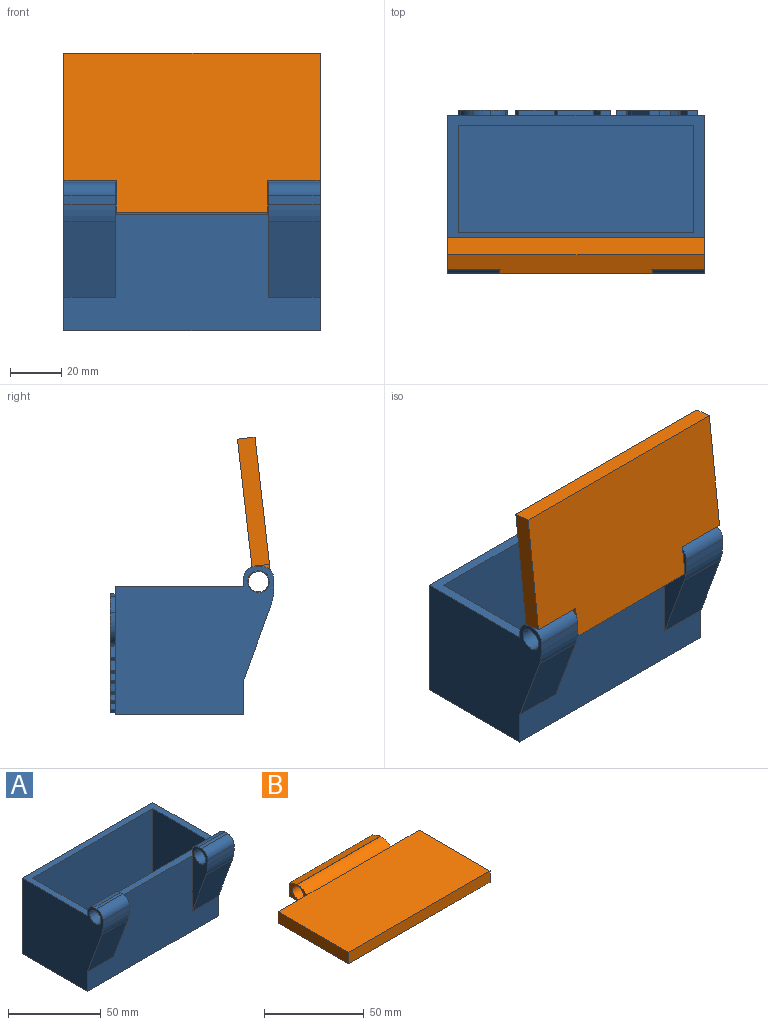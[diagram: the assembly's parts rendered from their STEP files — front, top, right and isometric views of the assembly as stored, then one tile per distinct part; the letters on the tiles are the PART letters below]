
ASSEMBLY  parts=2 mates=1
PART A: 93 faces, bbox 100x64x58 mm
  f0: plane 62x58mm, normal (-1,0,0), area 2773.6mm2, adj f1,f3,f4,f5,f10,f11,f13,f19
  f1: plane 100x50mm, normal (0,0,-1), area 5000mm2, adj f0,f2,f4,f5
  f2: plane 62x58mm, normal (1,0,0), area 2773.6mm2, adj f1,f3,f4,f5,f6,f8,f9,f20
  f3: plane 100x50mm, normal (0,0,1), area 1136mm2, adj f0,f2,f4,f5,f6,f10,f14,f15
  f4: plane 100x50mm, normal (0,-1,0), area 3521.2mm2, adj f0,f1,f2,f3,f7,f12,f21,f22
  f5: plane 100x50mm, normal (0,1,0), area 4050.1mm2, adj f0,f1,f2,f3,f29,f30,f31,f32
  f6: plane 20x3mm, normal (0,1,0), area 60mm2, adj f2,f3,f7,f28
  f7: plane 44.97x12mm, normal (-1,0,0), area 273.6mm2, adj f4,f6,f8,f9,f20,f22,f24,f27
  f8: plane 20x3.47mm, normal (0,-1,0), area 69.5mm2, adj f2,f7,f24,f27
  f9: plane 20x2mm, normal (0,0,1), area 40mm2, adj f2,f7,f27,f28
  f10: plane 20x3mm, normal (0,1,0), area 60mm2, adj f0,f3,f12,f26
  f11: plane 20x3.47mm, normal (0,-1,0), area 69.5mm2, adj f0,f12,f23,f25
  f12: plane 44.97x12mm, normal (1,0,0), area 273.6mm2, adj f4,f10,f11,f13,f19,f21,f23,f25
  f13: plane 20x2mm, normal (0,0,1), area 40mm2, adj f0,f12,f25,f26
  f14: plane 92x46mm, normal (0,-1,0), area 4232mm2, adj f3,f16,f17,f18
  f15: plane 92x46mm, normal (0,1,0), area 4232mm2, adj f3,f16,f17,f18
  f16: plane 46x42mm, normal (-1,0,0), area 1932mm2, adj f3,f14,f15,f17
  f17: plane 92x42mm, normal (0,0,1), area 3864mm2, adj f14,f15,f16,f18
  f18: plane 46x42mm, normal (1,0,0), area 1932mm2, adj f3,f14,f15,f17
  f19: cylinder r=4.25mm len=20mm, axis (1,0,0), area 534.1mm2, adj f0,f12
  f20: cylinder r=4.25mm len=20mm, axis (1,0,0), area 534.1mm2, adj f2,f7
  f21: plane 29.66x20mm, normal (0,-0.94,-0.34), area 631.2mm2, adj f0,f4,f12,f23
  f22: plane 29.66x20mm, normal (0,-0.94,-0.34), area 631.2mm2, adj f2,f4,f7,f24
  f23: cylinder r=20mm len=20mm, axis (1,0,0), area 139.6mm2, adj f0,f11,f12,f21
  f24: cylinder r=20mm len=20mm, axis (1,0,0), area 139.6mm2, adj f2,f7,f8,f22
  f25: cylinder r=5mm len=20mm, axis (-1,0,0), area 157.1mm2, adj f0,f11,f12,f13
  f26: cylinder r=5mm len=20mm, axis (1,0,0), area 157.1mm2, adj f0,f10,f12,f13
  f27: cylinder r=5mm len=20mm, axis (-1,0,0), area 157.1mm2, adj f2,f7,f8,f9
  f28: cylinder r=5mm len=20mm, axis (1,0,0), area 157.1mm2, adj f2,f6,f7,f9
  f29: plane 9.98x8.17mm, normal (-0.63,0,0.77), area 25.8mm2, adj f5,f30,f41,f42
  f30: plane 10.38x3.74mm, normal (-0.94,0,-0.34), area 22.1mm2, adj f5,f29,f31,f42
  f31: plane 4.37x2mm, normal (0.32,0,0.95), area 9.2mm2, adj f5,f30,f32,f42
  f32: plane 7.99x2.92mm, normal (0.94,0,0.34), area 17mm2, adj f5,f31,f33,f42
  f33: plane 2.7x2mm, normal (0.96,0,0.29), area 5.6mm2, adj f5,f32,f34,f42
  f34: plane 8.5x2.83mm, normal (-0.95,0,0.32), area 17.9mm2, adj f5,f33,f35,f42
  f35: plane 3.94x2mm, normal (0.32,0,0.95), area 8.3mm2, adj f5,f34,f36,f42
  f36: plane 18.56x6.19mm, normal (0.95,0,-0.32), area 39.1mm2, adj f5,f35,f37,f42
  f37: plane 3.94x2mm, normal (-0.32,0,-0.95), area 8.3mm2, adj f5,f36,f38,f42
  f38: plane 6.63x2.21mm, normal (-0.95,0,0.32), area 14mm2, adj f5,f37,f39,f42
  f39: plane 2x1.75mm, normal (-0.81,0,-0.59), area 4.3mm2, adj f5,f38,f40,f42
  f40: plane 7.47x6.2mm, normal (0.64,0,-0.77), area 19.4mm2, adj f5,f39,f41,f42
  f41: plane 4.47x2mm, normal (-0.32,0,-0.95), area 9.4mm2, adj f5,f29,f40,f42
  f42: plane 23.53x21.12mm, normal (0,1,0), area 175.6mm2, adj f29,f30,f31,f32,f33,f34,f35,f36
  f43: plane 12.22x2mm, normal (1,0,-0.01), area 24.4mm2, adj f5,f44,f52,f53
  f44: extruded ~4.41x2mm, area 8.9mm2, adj f5,f43,f45,f53
  f45: extruded ~2x1.68mm, area 3.9mm2, adj f5,f44,f46,f53
  f46: extruded ~2.08x2mm, area 5mm2, adj f5,f45,f47,f53
  f47: plane 9.88x7.18mm, normal (-0.81,0,0.59), area 24.4mm2, adj f5,f46,f48,f53
  f48: plane 3.97x2mm, normal (0.32,0,0.95), area 8.4mm2, adj f5,f47,f49,f53
  f49: plane 16.46x12.49mm, normal (0.8,0,-0.6), area 41.3mm2, adj f5,f48,f50,f53
  f50: plane 4.29x2mm, normal (-0.32,0,-0.95), area 9mm2, adj f5,f49,f51,f53
  f51: plane 20.67x2mm, normal (-1,0,-0.01), area 41.3mm2, adj f5,f50,f52,f53
  f52: plane 3.97x2mm, normal (0.32,0,0.95), area 8.4mm2, adj f5,f43,f51,f53
  f53: plane 22.1x16.9mm, normal (0,1,0), area 147.6mm2, adj f43,f44,f45,f46,f47,f48,f49,f50
  f54: plane 3.94x2mm, normal (-0.32,0,-0.95), area 8.3mm2, adj f5,f55,f57,f58
  f55: plane 18.56x6.19mm, normal (-0.95,0,0.32), area 39.1mm2, adj f5,f54,f56,f58
  f56: plane 3.94x2mm, normal (0.32,0,0.95), area 8.3mm2, adj f5,f55,f57,f58
  f57: plane 18.56x6.19mm, normal (0.95,0,-0.32), area 39.1mm2, adj f5,f54,f56,f58
  f58: plane 19.88x10.13mm, normal (0,1,0), area 81.2mm2, adj f54,f55,f56,f57
  f59: plane 15.29x5.1mm, normal (-0.95,0,0.32), area 32.2mm2, adj f5,f60,f66,f67
  f60: plane 5.04x2mm, normal (-0.32,0,-0.95), area 10.6mm2, adj f5,f59,f61,f67
  f61: plane 3.27x2mm, normal (-0.95,0,0.32), area 6.9mm2, adj f5,f60,f62,f67
  f62: plane 14.02x4.68mm, normal (0.32,0,0.95), area 29.6mm2, adj f5,f61,f63,f67
  f63: plane 3.27x2mm, normal (0.95,0,-0.32), area 6.9mm2, adj f5,f62,f64,f67
  f64: plane 5.04x2mm, normal (-0.32,0,-0.95), area 10.6mm2, adj f5,f63,f65,f67
  f65: plane 15.29x5.1mm, normal (0.95,0,-0.32), area 32.2mm2, adj f5,f64,f66,f67
  f66: plane 3.94x2mm, normal (-0.32,0,-0.95), area 8.3mm2, adj f5,f59,f65,f67
  f67: plane 21.56x15.17mm, normal (0,1,0), area 117.9mm2, adj f59,f60,f61,f62,f63,f64,f65,f66
  f68: plane 15.29x5.1mm, normal (-0.95,0,0.32), area 32.2mm2, adj f5,f69,f75,f76
  f69: plane 5.04x2mm, normal (-0.32,0,-0.95), area 10.6mm2, adj f5,f68,f70,f76
  f70: plane 3.27x2mm, normal (-0.95,0,0.32), area 6.9mm2, adj f5,f69,f71,f76
  f71: plane 14.02x4.68mm, normal (0.32,0,0.95), area 29.6mm2, adj f5,f70,f72,f76
  f72: plane 3.27x2mm, normal (0.95,0,-0.32), area 6.9mm2, adj f5,f71,f73,f76
  f73: plane 5.04x2mm, normal (-0.32,0,-0.95), area 10.6mm2, adj f5,f72,f74,f76
  f74: plane 15.29x5.1mm, normal (0.95,0,-0.32), area 32.2mm2, adj f5,f73,f75,f76
  f75: plane 3.94x2mm, normal (-0.32,0,-0.95), area 8.3mm2, adj f5,f68,f74,f76
  f76: plane 21.56x15.17mm, normal (0,1,0), area 117.9mm2, adj f68,f69,f70,f71,f72,f73,f74,f75
  f77: extruded ~6.33x4.63mm, area 16.1mm2, adj f5,f78,f90,f91
  f78: extruded ~7.37x2mm, area 15.2mm2, adj f5,f77,f79,f91
  f79: extruded ~5.75x4.64mm, area 15.2mm2, adj f5,f78,f80,f91
  f80: extruded ~7.84x2mm, area 16.1mm2, adj f5,f79,f81,f91
  f81: extruded ~6.35x4.66mm, area 16.1mm2, adj f5,f80,f82,f91
  f82: extruded ~7.38x2mm, area 15.2mm2, adj f5,f81,f83,f91
  f83: extruded ~5.73x4.66mm, area 15.2mm2, adj f5,f82,f90,f91
  f84: extruded ~5.09x2mm, area 10.4mm2, adj f85,f89,f91,f92
  f85: extruded ~3.01x2.76mm, area 8.5mm2, adj f84,f86,f91,f92
  f86: extruded ~6.78x5.02mm, area 18.8mm2, adj f85,f87,f91,f92
  f87: extruded ~7.83x3.26mm, area 18.8mm2, adj f86,f88,f91,f92
  f88: extruded ~4.05x2mm, area 8.5mm2, adj f87,f89,f91,f92
  f89: extruded ~4.29x2.74mm, area 10.4mm2, adj f84,f88,f91,f92
  f90: extruded ~7.85x2mm, area 16.1mm2, adj f5,f77,f83,f91
  f91: plane 21.03x19.88mm, normal (0,1,0), area 200.5mm2, adj f77,f78,f79,f80,f81,f82,f83,f84
  f92: plane 14.09x11.61mm, normal (0,1,0), area 109.2mm2, adj f84,f85,f86,f87,f88,f89
PART B: 14 faces, bbox 100x62.5x10 mm
  f0: plane 12.5x10mm, normal (1,0,0), area 62.8mm2, adj f1,f3,f4,f6,f11,f12,f13
  f1: plane 59x8mm, normal (0,1,0), area 472mm2, adj f0,f2,f4,f13
  f2: plane 12.5x10mm, normal (-1,0,0), area 62.8mm2, adj f1,f3,f4,f5,f11,f12,f13
  f3: plane 59x0.21mm, normal (0,0,1), area 12.3mm2, adj f0,f2,f12,f13
  f4: plane 100x62.5mm, normal (0,0,-1), area 5737.5mm2, adj f0,f1,f2,f5,f6,f7,f8,f9
  f5: plane 20.5x6.9mm, normal (0,1,0), area 141.4mm2, adj f2,f4,f7,f10
  f6: plane 20.5x6.9mm, normal (0,1,0), area 141.5mm2, adj f0,f4,f9,f10
  f7: plane 50x6.9mm, normal (-1,0,0), area 345mm2, adj f4,f5,f8,f10
  f8: plane 100x6.9mm, normal (0,-1,0), area 690mm2, adj f4,f7,f9,f10
  f9: plane 50x6.9mm, normal (1,0,0), area 345mm2, adj f4,f6,f8,f10
  f10: plane 100x50mm, normal (0,0,1), area 5000mm2, adj f5,f6,f7,f8,f9,f12
  f11: cylinder r=4mm len=59mm, axis (1,0,0), area 1482.8mm2, adj f0,f2
  f12: cylinder r=9mm len=59mm, axis (-1,0,0), area 454.5mm2, adj f0,f2,f3,f10
  f13: plane 59x5.5mm, normal (0,0.34,0.94), area 345mm2, adj f0,f1,f2,f3
PLACE A t=(0.07,0.14,-0.23)mm fixed
PLACE B rot(axis=(-1,0,0),96.5deg) t=(0.07,-57.3,83.38)mm
MATE revolute B.f11 <-> A.f19  axis (1,0,0) through (29.57,-55.86,51.77)mm
